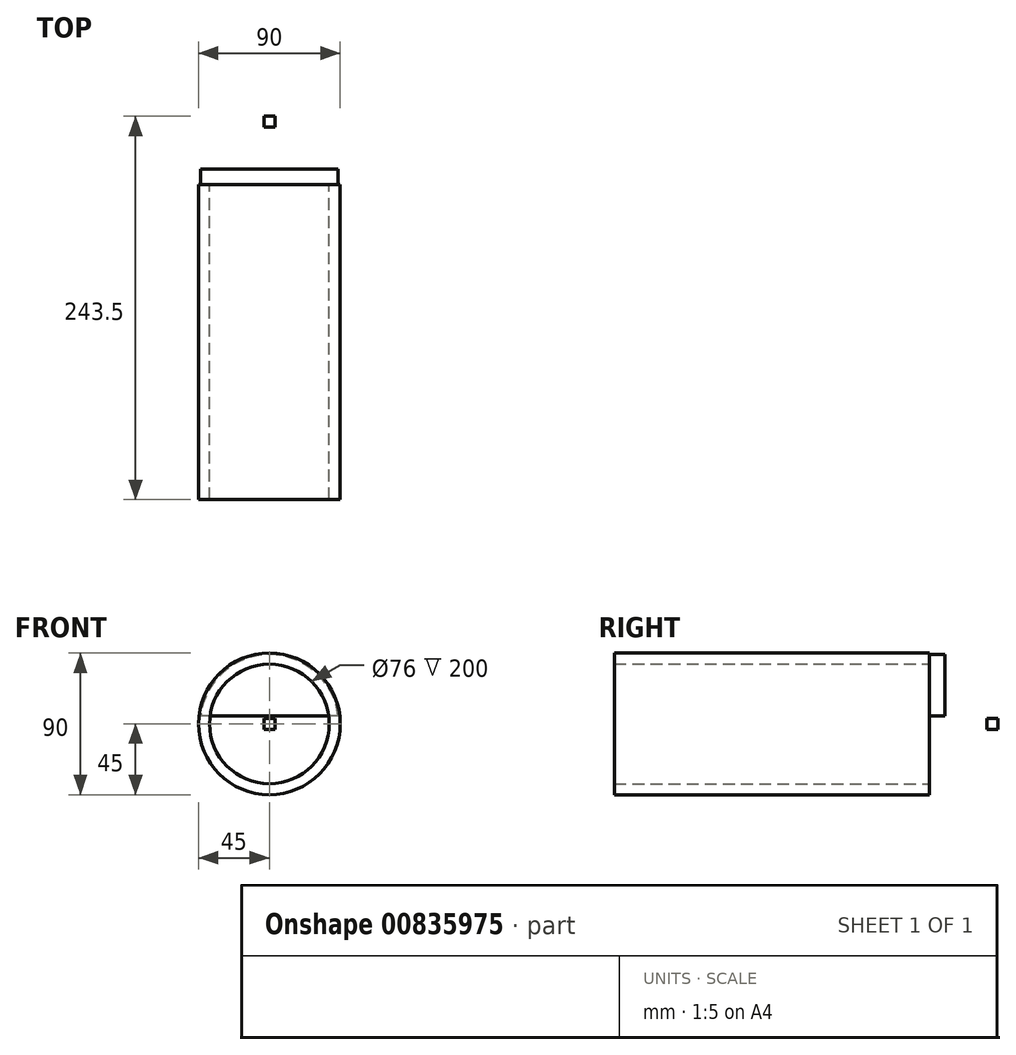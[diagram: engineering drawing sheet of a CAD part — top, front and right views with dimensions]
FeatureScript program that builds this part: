
annotation { "Feature Type Name" : "Feature", "Feature Type Description" : "" }
export const myFeature = defineFeature(function(context is Context, id is Id, definition is map)
    precondition{}
    {
        {
            var Q0;
            Q0=qCreatedBy(makeId("Front.planeOp"),FACE);
            var sketch = newSketch(context, id + "F0", { "sketchPlane" : qUnion([Q0])});
            skCircle(sketch, "E0", {"center": v(0, 0) * mm, "radius": 45 * mm});
            skCircle(sketch, "E1", {"center": v(0, 0) * mm, "radius": 38 * mm});
            skSolve(sketch);
        }
        {
            var Q0;
            Q0=qSketchRegion(id+"F0",true);
            extrude(context, id + "F1", {"entities" : qUnion([Q0]), "depth" : 200 * mm, "offsetDistance" : 25 * mm});
        }
        {
            var Q0;
            Q0=qCreatedBy(makeId("Right.planeOp"),FACE);
            var sketch = newSketch(context, id + "F2", { "sketchPlane" : qUnion([Q0])});
            skLineSegment(sketch, "E2", {"start": v(0, 0) * mm, "end": v(40, 0) * mm});
            skCircle(sketch, "E3", {"center": v(40, 0) * mm, "radius": 2.5 * mm});
            skSolve(sketch);
        }
        {
            var Q0;
            Q0=makeQuery(id+"F1.opExtrude","CAP_FACE",FACE,{"disambiguationData":[OSD([sQuery(id+"F0.wireOp",EDGE,"E0"),sQuery(id+"F0.wireOp",EDGE,"E1")])],"isStart":true});
            var sketch = newSketch(context, id + "F3", { "sketchPlane" : qUnion([Q0])});
            skLineSegment(sketch, "E4", {"start": v(0, 0) * mm, "end": v(0, 5) * mm});
            skLineSegment(sketch, "E5", {"start": v(0, 5) * mm, "end": v(43.71, 5) * mm});
            skLineSegment(sketch, "E6", {"start": v(0, 5) * mm, "end": v(-43.71, 5) * mm});
            skCircle(sketch, "E7", {"center": v(0, 0) * mm, "radius": 44 * mm});
            skSolve(sketch);
        }
        {
            var Q0;
            {var subQ0=sQuery(id+"F3.wireOp",EDGE,"E7");var subQ1=sQuery(id+"F3.wireOp",EDGE,"E5");var subQ2=makeQuery(id+"F3.imprint","INTERSECT",VERTEX,{"derivedFrom":[subQ1,subQ0]});Q0=makeQuery(id+"F3.imprint","IMPRINT",FACE,{"disambiguationData":[TD([[makeQuery(id+"F3.imprint","IMPRINT",EDGE,{"disambiguationData":[TD([[subQ2,1.0]])],"derivedFrom":subQ1}),1.0]])]});}
            var Q1;
            {var subQ0=sQuery(id+"F3.wireOp",EDGE,"E6");var subQ1=sQuery(id+"F3.wireOp",EDGE,"E5");var subQ2=makeQuery(id+"F3.imprint","INTERSECT",VERTEX,{"derivedFrom":[subQ1,subQ0]});Q1=makeQuery(id+"F3.imprint","IMPRINT",FACE,{"disambiguationData":[TD([[makeQuery(id+"F3.imprint","IMPRINT",EDGE,{"disambiguationData":[TD([[subQ2,-1.0]])],"derivedFrom":subQ1}),1.0]])]});}
            extrude(context, id + "F4", {"entities" : qUnion([Q0, Q1]), "depth" : 10 * mm, "offsetDistance" : 25 * mm});
        }
        {
            var Q0;
            Q0=qCreatedBy(makeId("Right.planeOp"),FACE);
            var sketch = newSketch(context, id + "F5", { "sketchPlane" : qUnion([Q0])});
            skLineSegment(sketch, "E8", {"start": v(0, 0) * mm, "end": v(40, 0) * mm});
            skLineSegment(sketch, "E9.bottom", {"start": v(36.5, -3.5) * mm, "end": v(43.5, -3.5) * mm});
            skLineSegment(sketch, "E9.top", {"start": v(36.5, 3.5) * mm, "end": v(43.5, 3.5) * mm});
            skLineSegment(sketch, "E9.left", {"start": v(36.5, -3.5) * mm, "end": v(36.5, 3.5) * mm});
            skLineSegment(sketch, "E9.right", {"start": v(43.5, -3.5) * mm, "end": v(43.5, 3.5) * mm});
            skPoint(sketch, "E9.middle", {"position": v(40, 0) * mm});
            skSolve(sketch);
        }
        {
            var Q0;
            {var subQ0=sQuery(id+"F5.wireOp",EDGE,"E9.bottom");Q0=makeQuery(id+"F5.imprint","IMPRINT",FACE,{"disambiguationData":[TD([[makeQuery(id+"F5.imprint","IMPRINT",EDGE,{"derivedFrom":subQ0}),1.0]])]});}
            extrude(context, id + "F6", {"entities" : qUnion([Q0]), "operationType" : NewBodyOperationType.ADD, "endBound" : BoundingType.SYMMETRIC, "depth" : 7 * mm, "offsetDistance" : 25 * mm});
        }
    });
